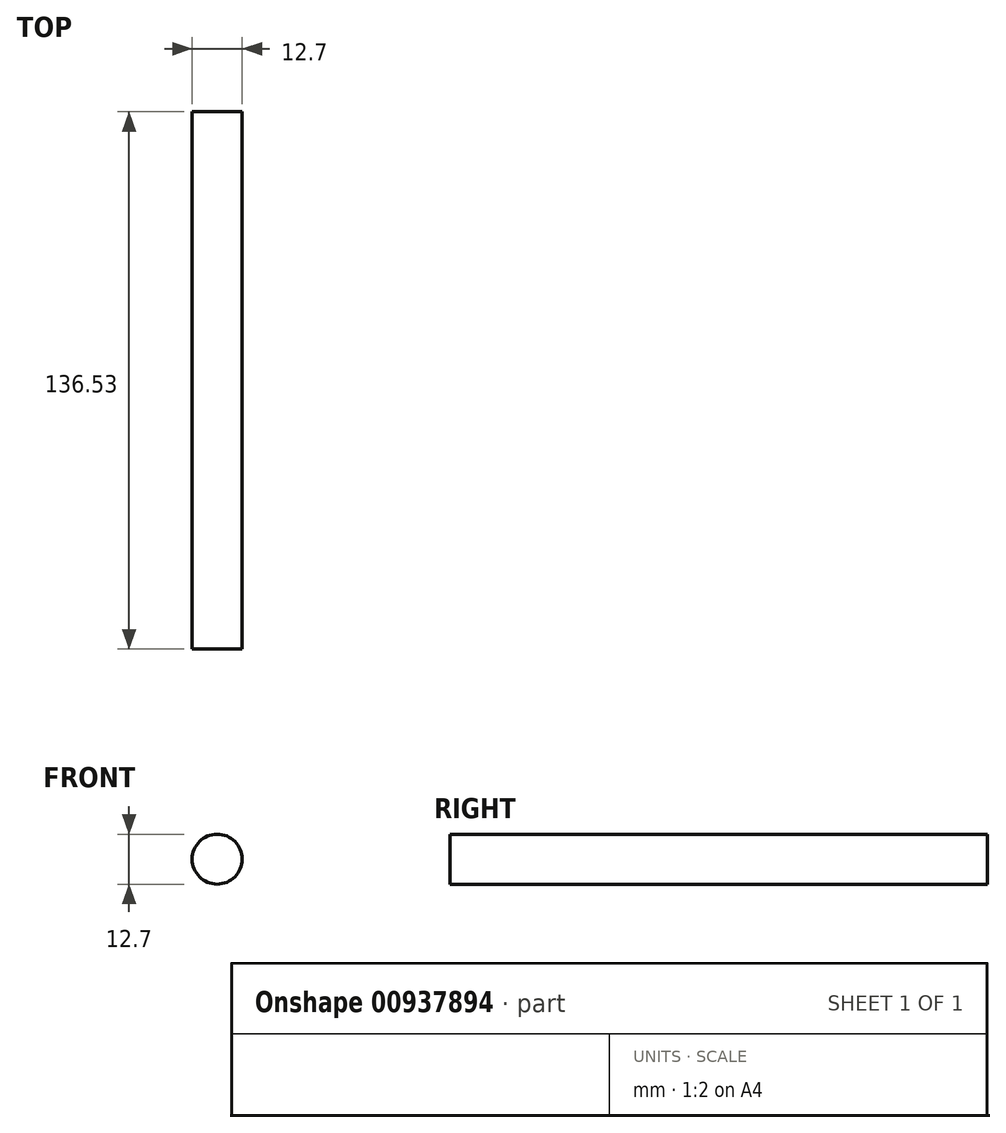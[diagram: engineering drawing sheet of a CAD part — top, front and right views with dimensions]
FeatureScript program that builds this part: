
annotation { "Feature Type Name" : "Feature", "Feature Type Description" : "" }
export const myFeature = defineFeature(function(context is Context, id is Id, definition is map)
    precondition{}
    {
        {
            var Q0;
            Q0=qCreatedBy(makeId("Front.planeOp"),FACE);
            var sketch = newSketch(context, id + "F0", { "sketchPlane" : qUnion([Q0])});
            skCircle(sketch, "E0", {"center": v(0, 0) * mm, "radius": 6.35 * mm});
            skSolve(sketch);
        }
        {
            var Q0;
            Q0=makeQuery(id+"F0.imprint","IMPRINT",FACE,{"disambiguationData":[TD([[makeQuery(id+"F0.imprint","IMPRINT",EDGE,{"derivedFrom":sQuery(id+"F0.wireOp",EDGE,"E0")}),1.0]])]});
            extrude(context, id + "F1", {"entities" : qUnion([Q0]), "depth" : 136.53 * mm, "offsetDistance" : 25.4 * mm});
        }
    });
